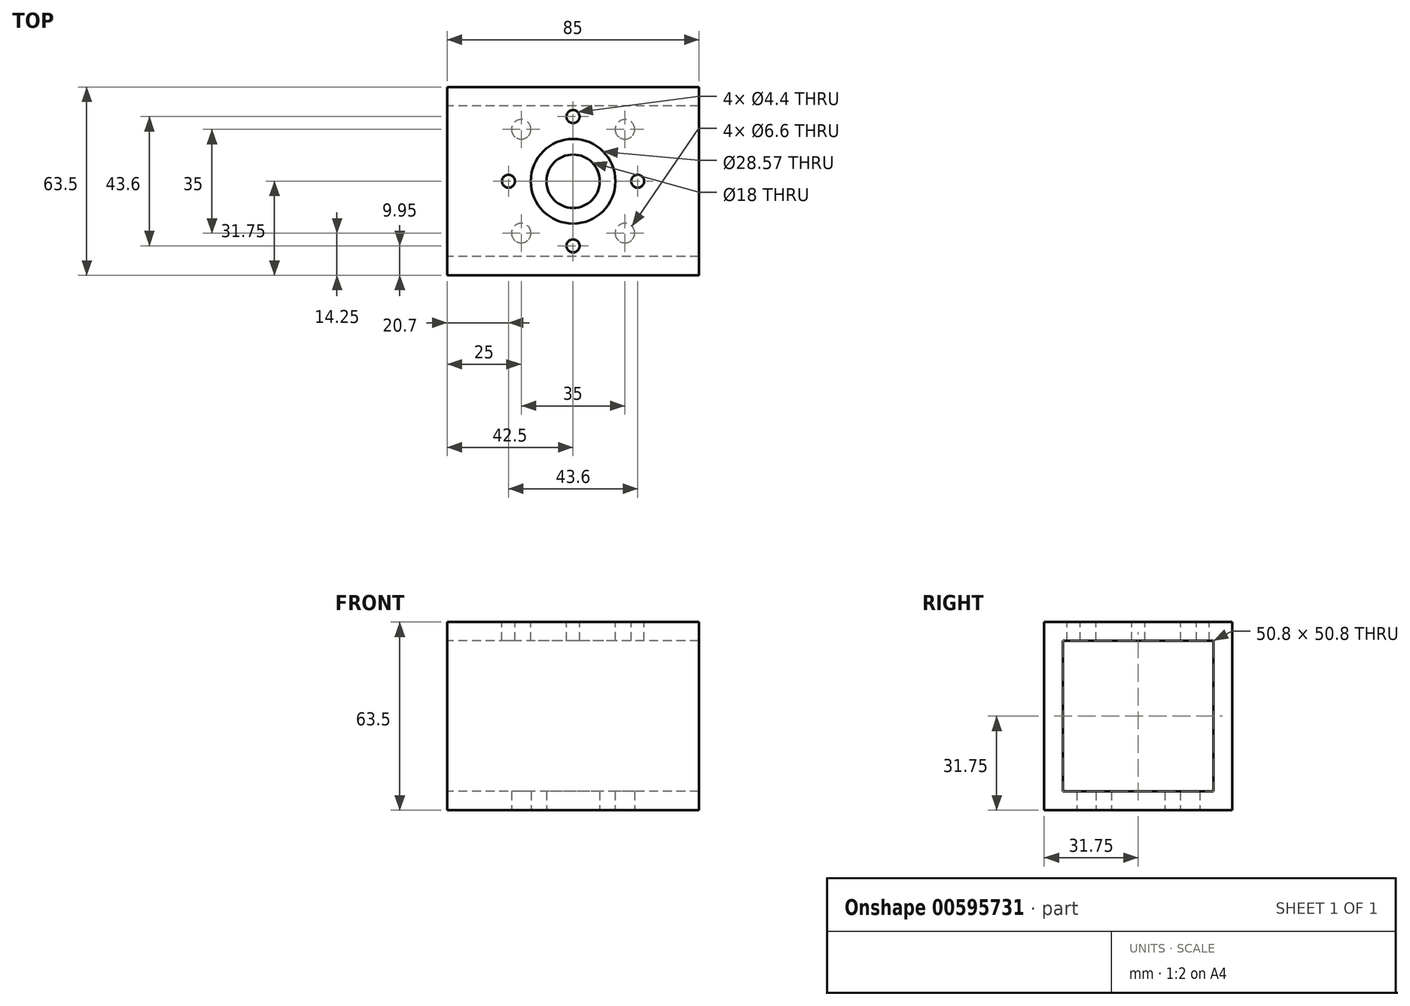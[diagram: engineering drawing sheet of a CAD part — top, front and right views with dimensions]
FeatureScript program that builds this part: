
annotation { "Feature Type Name" : "Feature", "Feature Type Description" : "" }
export const myFeature = defineFeature(function(context is Context, id is Id, definition is map)
    precondition{}
    {
        {
            var Q0;
            Q0=qCreatedBy(makeId("Right.planeOp"),FACE);
            var sketch = newSketch(context, id + "F0", { "sketchPlane" : qUnion([Q0])});
            skLineSegment(sketch, "E0.bottom", {"start": v(-25.4, 25.4) * mm, "end": v(25.4, 25.4) * mm});
            skLineSegment(sketch, "E0.top", {"start": v(-25.4, -25.4) * mm, "end": v(25.4, -25.4) * mm});
            skLineSegment(sketch, "E0.left", {"start": v(-25.4, 25.4) * mm, "end": v(-25.4, -25.4) * mm});
            skLineSegment(sketch, "E0.right", {"start": v(25.4, 25.4) * mm, "end": v(25.4, -25.4) * mm});
            skPoint(sketch, "E0.middle", {"position": v(0, 0) * mm});
            skLineSegment(sketch, "E1.bottom", {"start": v(-31.75, 31.75) * mm, "end": v(31.75, 31.75) * mm});
            skLineSegment(sketch, "E1.top", {"start": v(-31.75, -31.75) * mm, "end": v(31.75, -31.75) * mm});
            skLineSegment(sketch, "E1.left", {"start": v(-31.75, 31.75) * mm, "end": v(-31.75, -31.75) * mm});
            skLineSegment(sketch, "E1.right", {"start": v(31.75, 31.75) * mm, "end": v(31.75, -31.75) * mm});
            skSolve(sketch);
        }
        {
            var Q0;
            Q0=makeQuery(id+"F0.imprint","IMPRINT",FACE,{"disambiguationData":[TD([[makeQuery(id+"F0.imprint","IMPRINT",EDGE,{"derivedFrom":sQuery(id+"F0.wireOp",EDGE,"E0.bottom")}),1.0]])]});
            extrude(context, id + "F1", {"entities" : qUnion([Q0]), "depth" : 42.5 * mm, "offsetDistance" : 25 * mm, "hasSecondDirection" : true, "secondDirectionOppositeDirection" : true, "secondDirectionDepth" : 42.5 * mm});
        }
        {
            var Q0;
            Q0=makeQuery(id+"F1.opExtrude","SWEPT_FACE",FACE,{"disambiguationData":[OSD([sQuery(id+"F0.wireOp",EDGE,"E1.bottom")])]});
            var sketch = newSketch(context, id + "F2", { "sketchPlane" : qUnion([Q0])});
            skCircle(sketch, "E2", {"center": v(0, 0) * mm, "radius": 21.8 * mm, "construction": true});
            skPoint(sketch, "E3", {"position": v(-21.8, 0) * mm});
            skPoint(sketch, "E4", {"position": v(0, 21.8) * mm});
            skPoint(sketch, "E5", {"position": v(0, -21.8) * mm});
            skPoint(sketch, "E6", {"position": v(21.8, 0) * mm});
            skSolve(sketch);
        }
        {
            var Q0;
            Q0=sQuery(id+"F2.wireOp",VERTEX,"E3");
            var Q1;
            Q1=sQuery(id+"F2.wireOp",VERTEX,"E5");
            var Q2;
            Q2=sQuery(id+"F2.wireOp",VERTEX,"E6");
            var Q3;
            Q3=sQuery(id+"F2.wireOp",VERTEX,"E4");
            var Q4;
            Q4=makeQuery(id+"F1.opExtrude","SWEPT_BODY",BODY,{"disambiguationData":[OSD([sQuery(id+"F0.wireOp",EDGE,"E0.bottom"),sQuery(id+"F0.wireOp",EDGE,"E0.top"),sQuery(id+"F0.wireOp",EDGE,"E0.left"),sQuery(id+"F0.wireOp",EDGE,"E0.right"),sQuery(id+"F0.wireOp",EDGE,"E1.bottom"),sQuery(id+"F0.wireOp",EDGE,"E1.top"),sQuery(id+"F0.wireOp",EDGE,"E1.left"),sQuery(id+"F0.wireOp",EDGE,"E1.right")])]});
            hole(context, id + "F3", {"style" : HoleStyle.SIMPLE, "endStyle" : HoleEndStyle.BLIND, "standardTappedOrClearance" : lookupTablePath({ "standard" : "ISO", "fit" : "Normal", "size" : "M4", "type" : "Clearance" }), "standardBlindInLast" : lookupTablePath({ "fit" : "Standard", "standard" : "ISO", "size" : "M4", "type" : "Clearance" }), "holeDiameter" : 4.4 * mm, "majorDiameter" : 4 * mm, "holeDepth" : 14.1 * mm, "isTappedThrough" : true, "tappedDepth" : 12 * mm, "tapClearance" : 3, "locations" : qUnion([Q0, Q1, Q2, Q3]), "scope" : qUnion([Q4])});
        }
        {
            var Q0;
            Q0=makeQuery(id+"F1.opExtrude","SWEPT_FACE",FACE,{"disambiguationData":[OSD([sQuery(id+"F0.wireOp",EDGE,"E1.bottom")])]});
            var sketch = newSketch(context, id + "F4", { "sketchPlane" : qUnion([Q0])});
            skPoint(sketch, "E7", {"position": v(0, 0) * mm});
            skSolve(sketch);
        }
        {
            var Q0;
            Q0=sQuery(id+"F4.wireOp",VERTEX,"E7");
            var Q1;
            Q1=makeQuery(id+"F1.opExtrude","SWEPT_BODY",BODY,{"disambiguationData":[OSD([sQuery(id+"F0.wireOp",EDGE,"E0.bottom"),sQuery(id+"F0.wireOp",EDGE,"E0.top"),sQuery(id+"F0.wireOp",EDGE,"E0.left"),sQuery(id+"F0.wireOp",EDGE,"E0.right"),sQuery(id+"F0.wireOp",EDGE,"E1.bottom"),sQuery(id+"F0.wireOp",EDGE,"E1.top"),sQuery(id+"F0.wireOp",EDGE,"E1.left"),sQuery(id+"F0.wireOp",EDGE,"E1.right")])]});
            hole(context, id + "F5", {"style" : HoleStyle.SIMPLE, "endStyle" : HoleEndStyle.BLIND, "holeDiameter" : 28.57 * mm, "majorDiameter" : 5 * mm, "holeDepth" : 10 * mm, "isTappedThrough" : true, "tappedDepth" : 12 * mm, "tapClearance" : 3, "locations" : qUnion([Q0]), "scope" : qUnion([Q1])});
        }
        {
            var Q0;
            Q0=makeQuery(id+"F1.opExtrude","SWEPT_FACE",FACE,{"disambiguationData":[OSD([sQuery(id+"F0.wireOp",EDGE,"E1.top")])]});
            var sketch = newSketch(context, id + "F6", { "sketchPlane" : qUnion([Q0])});
            skLineSegment(sketch, "E8.bottom", {"start": v(-17.5, -17.5) * mm, "end": v(17.5, -17.5) * mm, "construction": true});
            skLineSegment(sketch, "E8.top", {"start": v(-17.5, 17.5) * mm, "end": v(17.5, 17.5) * mm, "construction": true});
            skLineSegment(sketch, "E8.left", {"start": v(-17.5, -17.5) * mm, "end": v(-17.5, 17.5) * mm, "construction": true});
            skLineSegment(sketch, "E8.right", {"start": v(17.5, -17.5) * mm, "end": v(17.5, 17.5) * mm, "construction": true});
            skPoint(sketch, "E8.middle", {"position": v(0, 0) * mm});
            skPoint(sketch, "E9", {"position": v(-17.5, -17.5) * mm});
            skPoint(sketch, "E10", {"position": v(-17.5, 17.5) * mm});
            skPoint(sketch, "E11", {"position": v(17.5, 17.5) * mm});
            skPoint(sketch, "E12", {"position": v(17.5, -17.5) * mm});
            skSolve(sketch);
        }
        {
            var Q0;
            Q0=sQuery(id+"F6.wireOp",VERTEX,"E9");
            var Q1;
            Q1=sQuery(id+"F6.wireOp",VERTEX,"E10");
            var Q2;
            Q2=sQuery(id+"F6.wireOp",VERTEX,"E11");
            var Q3;
            Q3=sQuery(id+"F6.wireOp",VERTEX,"E12");
            var Q4;
            Q4=makeQuery(id+"F1.opExtrude","SWEPT_BODY",BODY,{"disambiguationData":[OSD([sQuery(id+"F0.wireOp",EDGE,"E0.bottom"),sQuery(id+"F0.wireOp",EDGE,"E0.top"),sQuery(id+"F0.wireOp",EDGE,"E0.left"),sQuery(id+"F0.wireOp",EDGE,"E0.right"),sQuery(id+"F0.wireOp",EDGE,"E1.bottom"),sQuery(id+"F0.wireOp",EDGE,"E1.top"),sQuery(id+"F0.wireOp",EDGE,"E1.left"),sQuery(id+"F0.wireOp",EDGE,"E1.right")])]});
            hole(context, id + "F7", {"style" : HoleStyle.SIMPLE, "endStyle" : HoleEndStyle.BLIND, "standardTappedOrClearance" : lookupTablePath({ "standard" : "ISO", "fit" : "Normal", "size" : "M6", "type" : "Clearance" }), "standardBlindInLast" : lookupTablePath({ "fit" : "Standard", "standard" : "ISO", "size" : "M6", "type" : "Clearance" }), "holeDiameter" : 6.6 * mm, "majorDiameter" : 5 * mm, "holeDepth" : 10 * mm, "isTappedThrough" : true, "tappedDepth" : 12 * mm, "tapClearance" : 3, "locations" : qUnion([Q0, Q1, Q2, Q3]), "scope" : qUnion([Q4])});
        }
        {
            var Q0;
            Q0=makeQuery(id+"F1.opExtrude","SWEPT_FACE",FACE,{"disambiguationData":[OSD([sQuery(id+"F0.wireOp",EDGE,"E1.top")])]});
            var sketch = newSketch(context, id + "F8", { "sketchPlane" : qUnion([Q0])});
            skPoint(sketch, "E13", {"position": v(0, 0) * mm});
            skSolve(sketch);
        }
        {
            var Q0;
            Q0=sQuery(id+"F8.wireOp",VERTEX,"E13");
            var Q1;
            Q1=makeQuery(id+"F1.opExtrude","SWEPT_BODY",BODY,{"disambiguationData":[OSD([sQuery(id+"F0.wireOp",EDGE,"E0.bottom"),sQuery(id+"F0.wireOp",EDGE,"E0.top"),sQuery(id+"F0.wireOp",EDGE,"E0.left"),sQuery(id+"F0.wireOp",EDGE,"E0.right"),sQuery(id+"F0.wireOp",EDGE,"E1.bottom"),sQuery(id+"F0.wireOp",EDGE,"E1.top"),sQuery(id+"F0.wireOp",EDGE,"E1.left"),sQuery(id+"F0.wireOp",EDGE,"E1.right")])]});
            hole(context, id + "F9", {"style" : HoleStyle.SIMPLE, "endStyle" : HoleEndStyle.BLIND, "holeDiameter" : 18 * mm, "majorDiameter" : 5 * mm, "holeDepth" : 10 * mm, "isTappedThrough" : true, "tappedDepth" : 12 * mm, "tapClearance" : 3, "locations" : qUnion([Q0]), "scope" : qUnion([Q1])});
        }
    });
